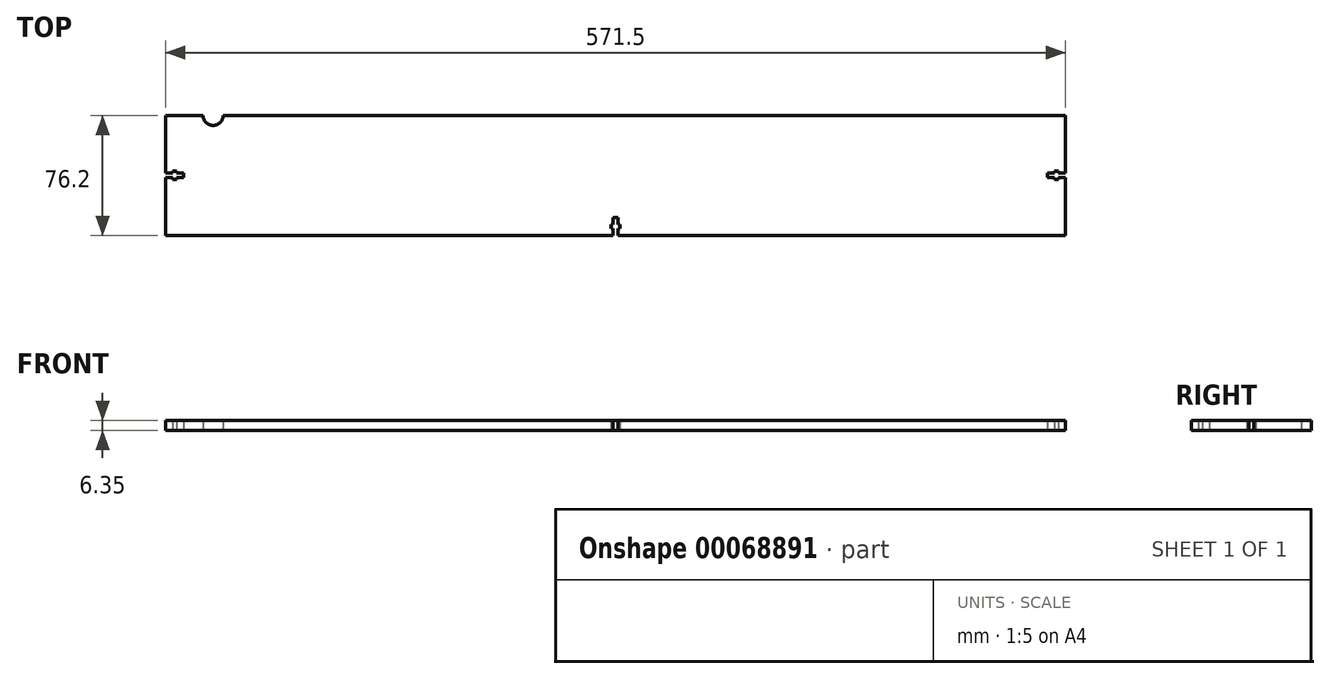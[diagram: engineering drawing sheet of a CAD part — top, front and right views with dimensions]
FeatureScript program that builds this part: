
annotation { "Feature Type Name" : "Feature", "Feature Type Description" : "" }
export const myFeature = defineFeature(function(context is Context, id is Id, definition is map)
    precondition{}
    {
        {
            var Q0;
            Q0=qCreatedBy(makeId("Top.planeOp"),FACE);
            var sketch = newSketch(context, id + "F0", { "sketchPlane" : qUnion([Q0])});
            skLineSegment(sketch, "E0.rect.bottom", {"start": v(285.75, -38.1) * mm, "end": v(1.46, -38.1) * mm});
            skLineSegment(sketch, "E0.rect.top", {"start": v(285.75, 38.1) * mm, "end": v(-249.25, 38.1) * mm});
            skLineSegment(sketch, "E0.rect.left", {"start": v(285.75, -38.1) * mm, "end": v(285.75, -1.46) * mm});
            skLineSegment(sketch, "E0.rect.right", {"start": v(-285.75, -38.1) * mm, "end": v(-285.75, -1.46) * mm});
            skPoint(sketch, "E0.rect.middle", {"position": v(0, 0) * mm});
            skLineSegment(sketch, "E1", {"start": v(0, 38.1) * mm, "end": v(0, -38.1) * mm, "construction": true});
            skLineSegment(sketch, "E2", {"start": v(-285.75, 0) * mm, "end": v(285.75, 0) * mm, "construction": true});
            skLineSegment(sketch, "E3.0", {"start": v(-1.46, 38.1) * mm, "end": v(-1.46, -38.1) * mm, "construction": true});
            skLineSegment(sketch, "E4", {"start": v(-1.46, -38.1) * mm, "end": v(-1.46, -33.66) * mm});
            skLineSegment(sketch, "E5", {"start": v(-1.46, -33.66) * mm, "end": v(-2.73, -33.66) * mm});
            skLineSegment(sketch, "E6", {"start": v(-2.73, -33.66) * mm, "end": v(-2.73, -31.12) * mm});
            skLineSegment(sketch, "E7", {"start": v(-2.73, -31.12) * mm, "end": v(-1.46, -31.12) * mm});
            skLineSegment(sketch, "E8", {"start": v(-1.46, -31.12) * mm, "end": v(-1.46, -26.67) * mm});
            skLineSegment(sketch, "E9", {"start": v(-1.46, -26.67) * mm, "end": v(0, -26.67) * mm});
            skLineSegment(sketch, "E10.MirrorCS", {"start": v(1.46, -26.67) * mm, "end": v(0, -26.67) * mm});
            skLineSegment(sketch, "E11.MirrorCS", {"start": v(1.46, -31.12) * mm, "end": v(1.46, -26.67) * mm});
            skLineSegment(sketch, "E12.MirrorCS", {"start": v(2.73, -31.12) * mm, "end": v(1.46, -31.12) * mm});
            skLineSegment(sketch, "E13.MirrorCS", {"start": v(2.73, -33.66) * mm, "end": v(2.73, -31.12) * mm});
            skLineSegment(sketch, "E14.MirrorCS", {"start": v(1.46, -33.66) * mm, "end": v(2.73, -33.66) * mm});
            skLineSegment(sketch, "E15.MirrorCS", {"start": v(1.46, -38.1) * mm, "end": v(1.46, -33.66) * mm});
            skLineSegment(sketch, "E16.trimOffspring", {"start": v(-1.46, -38.1) * mm, "end": v(-285.75, -38.1) * mm});
            skLineSegment(sketch, "E17.0", {"start": v(-285.75, -1.46) * mm, "end": v(298.45, -1.46) * mm, "construction": true});
            skLineSegment(sketch, "E18", {"start": v(-285.75, -1.46) * mm, "end": v(-281.3, -1.46) * mm});
            skLineSegment(sketch, "E19", {"start": v(-281.3, -1.46) * mm, "end": v(-281.3, -2.73) * mm});
            skLineSegment(sketch, "E20", {"start": v(-281.3, -2.73) * mm, "end": v(-278.77, -2.73) * mm});
            skLineSegment(sketch, "E21", {"start": v(-278.77, -2.73) * mm, "end": v(-278.77, -1.46) * mm});
            skLineSegment(sketch, "E22", {"start": v(-278.76, -1.46) * mm, "end": v(-274.32, -1.46) * mm});
            skLineSegment(sketch, "E23", {"start": v(-274.32, -1.46) * mm, "end": v(-274.32, 0) * mm});
            skLineSegment(sketch, "E24.MirrorCS", {"start": v(-274.32, 1.46) * mm, "end": v(-274.32, 0) * mm});
            skLineSegment(sketch, "E25.MirrorCS", {"start": v(-278.76, 1.46) * mm, "end": v(-274.32, 1.46) * mm});
            skLineSegment(sketch, "E26.MirrorCS", {"start": v(-278.77, 2.73) * mm, "end": v(-278.77, 1.46) * mm});
            skLineSegment(sketch, "E27.MirrorCS", {"start": v(-281.3, 2.73) * mm, "end": v(-278.77, 2.73) * mm});
            skLineSegment(sketch, "E28.MirrorCS", {"start": v(-281.3, 1.46) * mm, "end": v(-281.3, 2.73) * mm});
            skLineSegment(sketch, "E29.MirrorCS", {"start": v(-285.75, 1.46) * mm, "end": v(-281.3, 1.46) * mm});
            skLineSegment(sketch, "E30.MirrorCS", {"start": v(285.75, -1.46) * mm, "end": v(281.3, -1.46) * mm});
            skLineSegment(sketch, "E31.MirrorCS", {"start": v(281.3, -1.46) * mm, "end": v(281.3, -2.73) * mm});
            skLineSegment(sketch, "E32.MirrorCS", {"start": v(281.3, -2.73) * mm, "end": v(278.77, -2.73) * mm});
            skLineSegment(sketch, "E33.MirrorCS", {"start": v(278.77, -2.73) * mm, "end": v(278.77, -1.46) * mm});
            skLineSegment(sketch, "E34.MirrorCS", {"start": v(278.76, -1.46) * mm, "end": v(274.32, -1.46) * mm});
            skLineSegment(sketch, "E35.MirrorCS", {"start": v(274.32, -1.46) * mm, "end": v(274.32, 0) * mm});
            skLineSegment(sketch, "E36.MirrorCS", {"start": v(274.32, 1.46) * mm, "end": v(274.32, 0) * mm});
            skLineSegment(sketch, "E37.MirrorCS", {"start": v(278.76, 1.46) * mm, "end": v(274.32, 1.46) * mm});
            skLineSegment(sketch, "E38.MirrorCS", {"start": v(278.77, 2.73) * mm, "end": v(278.77, 1.46) * mm});
            skLineSegment(sketch, "E39.MirrorCS", {"start": v(281.3, 2.73) * mm, "end": v(278.77, 2.73) * mm});
            skLineSegment(sketch, "E40.MirrorCS", {"start": v(281.3, 1.46) * mm, "end": v(281.3, 2.73) * mm});
            skLineSegment(sketch, "E41.MirrorCS", {"start": v(285.75, 1.46) * mm, "end": v(281.3, 1.46) * mm});
            skLineSegment(sketch, "E42.trimOffspring", {"start": v(285.75, 1.46) * mm, "end": v(285.75, 38.1) * mm});
            skLineSegment(sketch, "E43.trimOffspring", {"start": v(-285.75, 1.46) * mm, "end": v(-285.75, 38.1) * mm});
            skArc(sketch, "E44", {"start": v(-261.95, 38.1) * mm, "mid": v(-255.6, 31.75) * mm, "end": v(-249.25, 38.1) * mm});
            skLineSegment(sketch, "E45.trimOffspring", {"start": v(-261.95, 38.1) * mm, "end": v(-285.75, 38.1) * mm});
            skSolve(sketch);
        }
        {
            var Q0;
            Q0=makeQuery(id+"F0.imprint","IMPRINT",FACE,{"disambiguationData":[TD([[makeQuery(id+"F0.imprint","IMPRINT",EDGE,{"derivedFrom":sQuery(id+"F0.wireOp",EDGE,"E0.rect.bottom")}),-1.0]])]});
            extrude(context, id + "F1", {"entities" : qUnion([Q0]), "depth" : 6.35 * mm});
        }
    });
